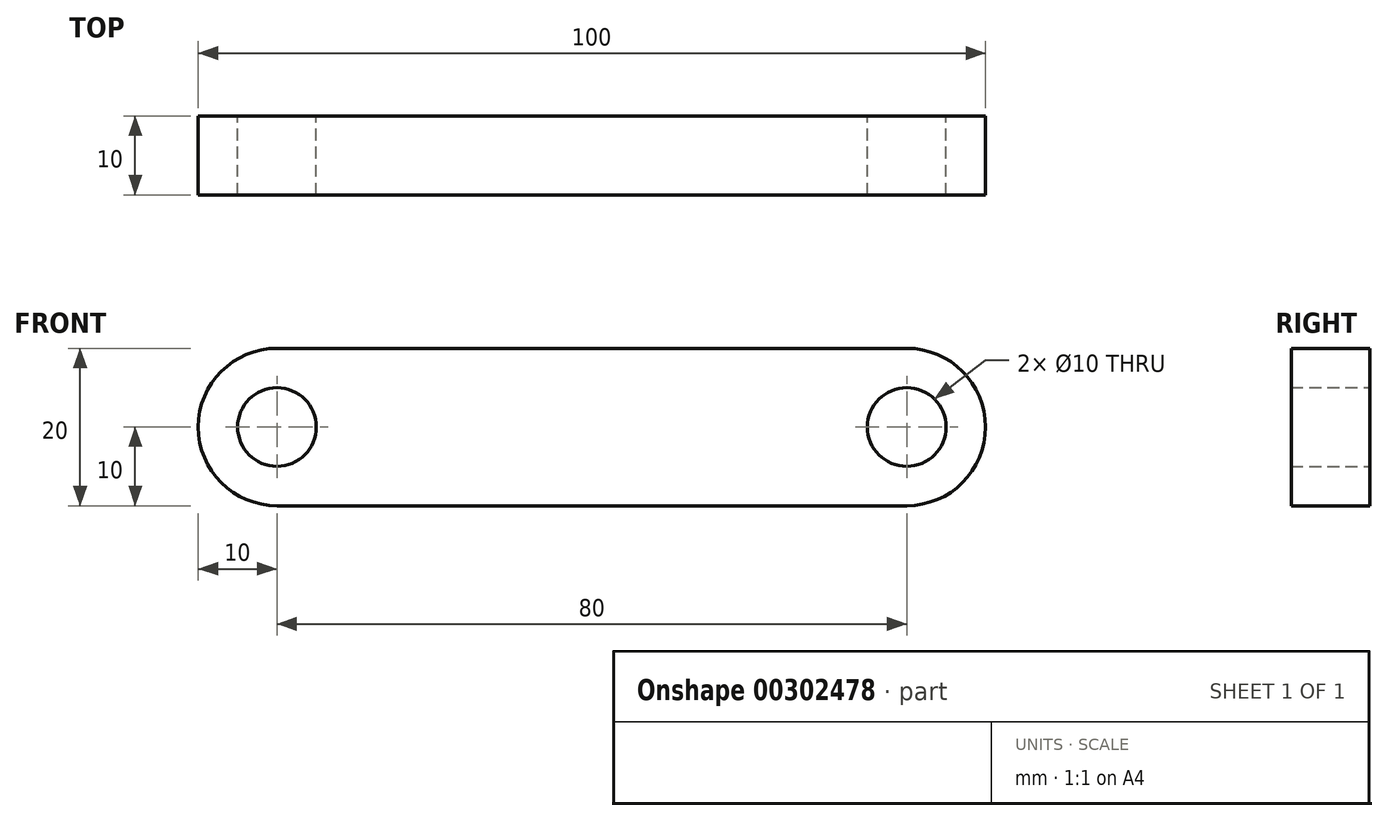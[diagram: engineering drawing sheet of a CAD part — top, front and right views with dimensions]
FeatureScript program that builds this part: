
annotation { "Feature Type Name" : "Feature", "Feature Type Description" : "" }
export const myFeature = defineFeature(function(context is Context, id is Id, definition is map)
    precondition{}
    {
        {
            var Q0;
            Q0=qCreatedBy(makeId("Front.planeOp"),FACE);
            var sketch = newSketch(context, id + "F0", { "sketchPlane" : qUnion([Q0])});
            skLineSegment(sketch, "E0", {"start": v(0, 0) * mm, "end": v(80, 0) * mm, "construction": true});
            skCircle(sketch, "E1", {"center": v(0, 0) * mm, "radius": 5 * mm});
            skCircle(sketch, "E2", {"center": v(80, 0) * mm, "radius": 5 * mm});
            skArc(sketch, "E3.0.startCap", {"start": v(0, -10) * mm, "mid": v(-10, 0) * mm, "end": v(0, 10) * mm});
            skArc(sketch, "E3.0.endCap", {"start": v(80, 10) * mm, "mid": v(90, 0) * mm, "end": v(80, -10) * mm});
            skLineSegment(sketch, "E3.0.left", {"start": v(0, 10) * mm, "end": v(80, 10) * mm});
            skLineSegment(sketch, "E3.0.right", {"start": v(0, -10) * mm, "end": v(80, -10) * mm});
            skSolve(sketch);
        }
        {
            var Q0;
            Q0 = qSketchRegion(id + "F0", true);
            extrude(context, id + "F1", {"entities" : qUnion([Q0]), "depth" : 10 * mm});
        }
    });
